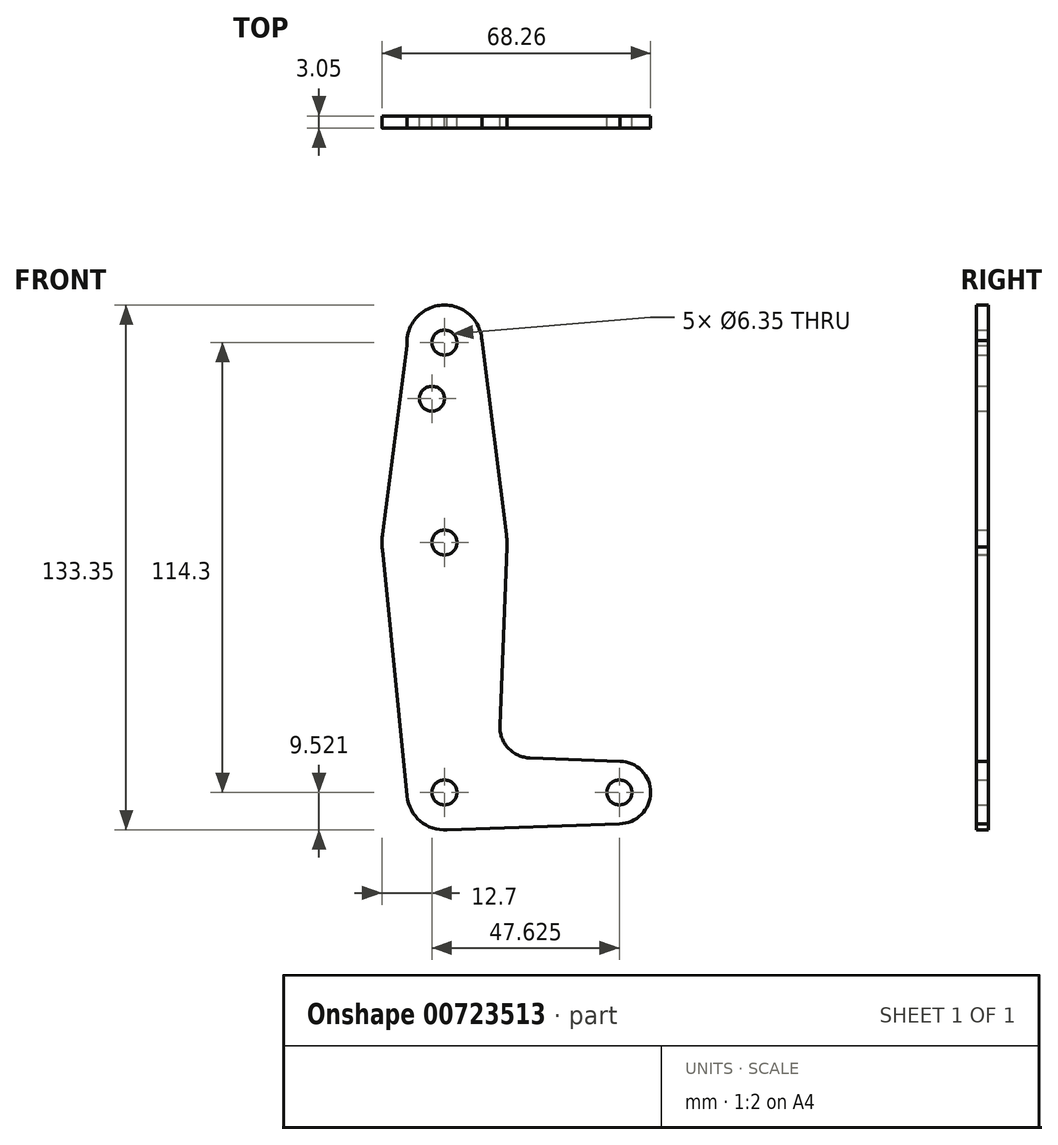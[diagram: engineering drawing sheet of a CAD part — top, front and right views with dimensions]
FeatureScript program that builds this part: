
annotation { "Feature Type Name" : "Feature", "Feature Type Description" : "" }
export const myFeature = defineFeature(function(context is Context, id is Id, definition is map)
    precondition{}
    {
        {
            var Q0;
            Q0=qCreatedBy(makeId("Front.planeOp"),FACE);
            var sketch = newSketch(context, id + "F0", { "sketchPlane" : qUnion([Q0])});
            skLineSegment(sketch, "E0", {"start": v(3.17, 116.12) * mm, "end": v(3.18, 1.82) * mm, "construction": true});
            skLineSegment(sketch, "E1", {"start": v(3.18, 1.82) * mm, "end": v(47.63, 1.82) * mm, "construction": true});
            skCircle(sketch, "E2", {"center": v(3.17, 116.12) * mm, "radius": 9.53 * mm});
            skCircle(sketch, "E3", {"center": v(3.18, 1.82) * mm, "radius": 9.53 * mm});
            skCircle(sketch, "E4", {"center": v(47.63, 1.82) * mm, "radius": 7.94 * mm});
            skCircle(sketch, "E5", {"center": v(3.18, 65.32) * mm, "radius": 15.88 * mm});
            skLineSegment(sketch, "E6", {"start": v(-6.32, 115.42) * mm, "end": v(-12.57, 67.37) * mm});
            skLineSegment(sketch, "E7", {"start": v(-12.7, 65.18) * mm, "end": v(-6.22, 0) * mm});
            skLineSegment(sketch, "E8", {"start": v(12.5, 118.06) * mm, "end": v(18.92, 67.37) * mm});
            skLineSegment(sketch, "E9", {"start": v(19.05, 65.18) * mm, "end": v(17.24, 18.83) * mm});
            skLineSegment(sketch, "E10", {"start": v(47.75, 9.76) * mm, "end": v(24.9, 10.57) * mm});
            skLineSegment(sketch, "E11", {"start": v(47.63, -6.12) * mm, "end": v(3.18, -7.7) * mm});
            skCircle(sketch, "E12", {"center": v(3.17, 116.12) * mm, "radius": 3.18 * mm});
            skCircle(sketch, "E13", {"center": v(3.18, 65.32) * mm, "radius": 3.18 * mm});
            skCircle(sketch, "E14", {"center": v(3.18, 1.82) * mm, "radius": 3.18 * mm});
            skCircle(sketch, "E15", {"center": v(47.63, 1.82) * mm, "radius": 3.18 * mm});
            skCircle(sketch, "E16", {"center": v(0, 101.85) * mm, "radius": 3.18 * mm});
            skPoint(sketch, "E17.newPointA", {"position": v(16.51, 0) * mm});
            skArc(sketch, "E17.filletArc", {"start": v(17.24, 18.83) * mm, "mid": v(19.36, 13.11) * mm, "end": v(24.9, 10.57) * mm});
            skSolve(sketch);
        }
        {
            var Q0;
            Q0 = qSketchRegion(id + "F0", true);
            extrude(context, id + "F1", {"entities" : qUnion([Q0]), "depth" : 3.05 * mm, "offsetDistance" : 25.4 * mm});
        }
    });
